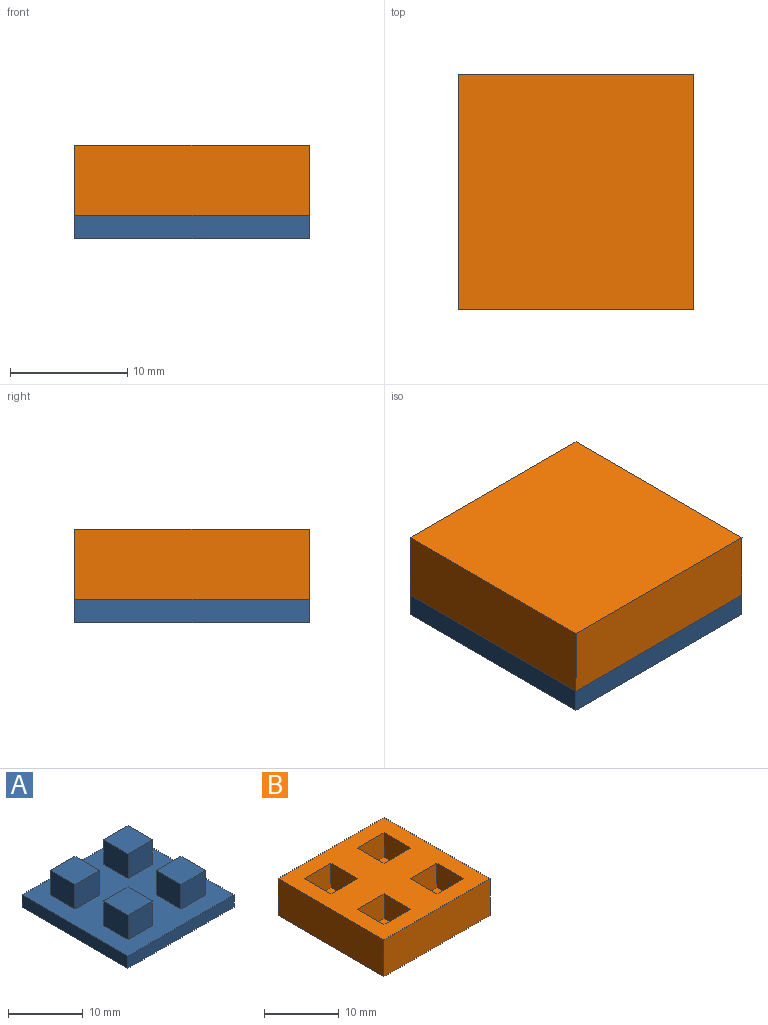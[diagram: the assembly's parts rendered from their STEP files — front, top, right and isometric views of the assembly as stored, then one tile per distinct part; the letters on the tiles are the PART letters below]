
ASSEMBLY  parts=2 mates=1
PART A: 26 faces, bbox 20x20x6 mm
  f0: plane 20x2mm, normal (1,0,0), area 40mm2, adj f1,f3,f4,f5
  f1: plane 20x2mm, normal (0,1,0), area 40mm2, adj f0,f2,f4,f5
  f2: plane 20x2mm, normal (-1,0,0), area 40mm2, adj f1,f3,f4,f5
  f3: plane 20x2mm, normal (0,-1,0), area 40mm2, adj f0,f2,f4,f5
  f4: plane 20x20mm, normal (0,0,1), area 315.4mm2, adj f0,f1,f2,f3,f7,f8,f9,f10
  f5: plane 20x20mm, normal (0,0,-1), area 400mm2, adj f0,f1,f2,f3
  f6: plane 4.6x4.6mm, normal (0,0,1), area 21.2mm2, adj f7,f8,f9,f10
  f7: plane 4.6x4mm, normal (1,0,0), area 18.4mm2, adj f4,f6,f8,f10
  f8: plane 4.6x4mm, normal (0,1,0), area 18.4mm2, adj f4,f6,f7,f9
  f9: plane 4.6x4mm, normal (-1,0,0), area 18.4mm2, adj f4,f6,f8,f10
  f10: plane 4.6x4mm, normal (0,-1,0), area 18.4mm2, adj f4,f6,f7,f9
  f11: plane 4.6x4.6mm, normal (0,0,1), area 21.2mm2, adj f12,f13,f14,f15
  f12: plane 4.6x4mm, normal (-1,0,0), area 18.4mm2, adj f4,f11,f13,f15
  f13: plane 4.6x4mm, normal (0,-1,0), area 18.4mm2, adj f4,f11,f12,f14
  f14: plane 4.6x4mm, normal (1,0,0), area 18.4mm2, adj f4,f11,f13,f15
  f15: plane 4.6x4mm, normal (0,1,0), area 18.4mm2, adj f4,f11,f12,f14
  f16: plane 4.6x4.6mm, normal (0,0,1), area 21.2mm2, adj f17,f18,f19,f20
  f17: plane 4.6x4mm, normal (1,0,0), area 18.4mm2, adj f4,f16,f18,f20
  f18: plane 4.6x4mm, normal (0,1,0), area 18.4mm2, adj f4,f16,f17,f19
  f19: plane 4.6x4mm, normal (-1,0,0), area 18.4mm2, adj f4,f16,f18,f20
  f20: plane 4.6x4mm, normal (0,-1,0), area 18.4mm2, adj f4,f16,f17,f19
  f21: plane 4.6x4.6mm, normal (0,0,1), area 21.2mm2, adj f22,f23,f24,f25
  f22: plane 4.6x4mm, normal (-1,0,0), area 18.4mm2, adj f4,f21,f23,f25
  f23: plane 4.6x4mm, normal (0,-1,0), area 18.4mm2, adj f4,f21,f22,f24
  f24: plane 4.6x4mm, normal (1,0,0), area 18.4mm2, adj f4,f21,f23,f25
  f25: plane 4.6x4mm, normal (0,1,0), area 18.4mm2, adj f4,f21,f22,f24
PART B: 26 faces, bbox 20x20x6 mm
  f0: plane 20x6mm, normal (1,0,0), area 120mm2, adj f1,f19,f20,f21
  f1: plane 20x6mm, normal (0,1,0), area 120mm2, adj f0,f2,f20,f21
  f2: plane 20x6mm, normal (-1,0,0), area 120mm2, adj f1,f19,f20,f21
  f3: plane 5x4mm, normal (0,1,0), area 20mm2, adj f4,f15,f20,f24
  f4: plane 5x4mm, normal (1,0,0), area 20mm2, adj f3,f5,f20,f24
  f5: plane 5x4mm, normal (0,-1,0), area 20mm2, adj f4,f15,f20,f24
  f6: plane 5x4mm, normal (0,1,0), area 20mm2, adj f7,f16,f20,f22
  f7: plane 5x4mm, normal (1,0,0), area 20mm2, adj f6,f8,f20,f22
  f8: plane 5x4mm, normal (0,-1,0), area 20mm2, adj f7,f16,f20,f22
  f9: plane 5x4mm, normal (0,-1,0), area 20mm2, adj f10,f17,f20,f23
  f10: plane 5x4mm, normal (-1,0,0), area 20mm2, adj f9,f11,f20,f23
  f11: plane 5x4mm, normal (0,1,0), area 20mm2, adj f10,f17,f20,f23
  f12: plane 5x4mm, normal (0,-1,0), area 20mm2, adj f13,f18,f20,f25
  f13: plane 5x4mm, normal (-1,0,0), area 20mm2, adj f12,f14,f20,f25
  f14: plane 5x4mm, normal (0,1,0), area 20mm2, adj f13,f18,f20,f25
  f15: plane 5x4mm, normal (-1,0,0), area 20mm2, adj f3,f5,f20,f24
  f16: plane 5x4mm, normal (-1,0,0), area 20mm2, adj f6,f8,f20,f22
  f17: plane 5x4mm, normal (1,0,0), area 20mm2, adj f9,f11,f20,f23
  f18: plane 5x4mm, normal (1,0,0), area 20mm2, adj f12,f14,f20,f25
  f19: plane 20x6mm, normal (0,-1,0), area 120mm2, adj f0,f2,f20,f21
  f20: plane 20x20mm, normal (0,0,1), area 300mm2, adj f0,f1,f2,f3,f4,f5,f6,f7
  f21: plane 20x20mm, normal (0,0,-1), area 400mm2, adj f0,f1,f2,f19
  f22: plane 5x5mm, normal (0,0,1), area 25mm2, adj f6,f7,f8,f16
  f23: plane 5x5mm, normal (0,0,1), area 25mm2, adj f9,f10,f11,f17
  f24: plane 5x5mm, normal (0,0,1), area 25mm2, adj f3,f4,f5,f15
  f25: plane 5x5mm, normal (0,0,1), area 25mm2, adj f12,f13,f14,f18
PLACE A t=(5.42,4.93,-1.07)mm
PLACE B rot(axis=(0.71,-0.71,0),180deg) t=(5.42,4.93,6.93)mm
MATE slider B.f20 <-> A.f4  axis (0,0,-1) through (5.42,4.93,0.93)mm
